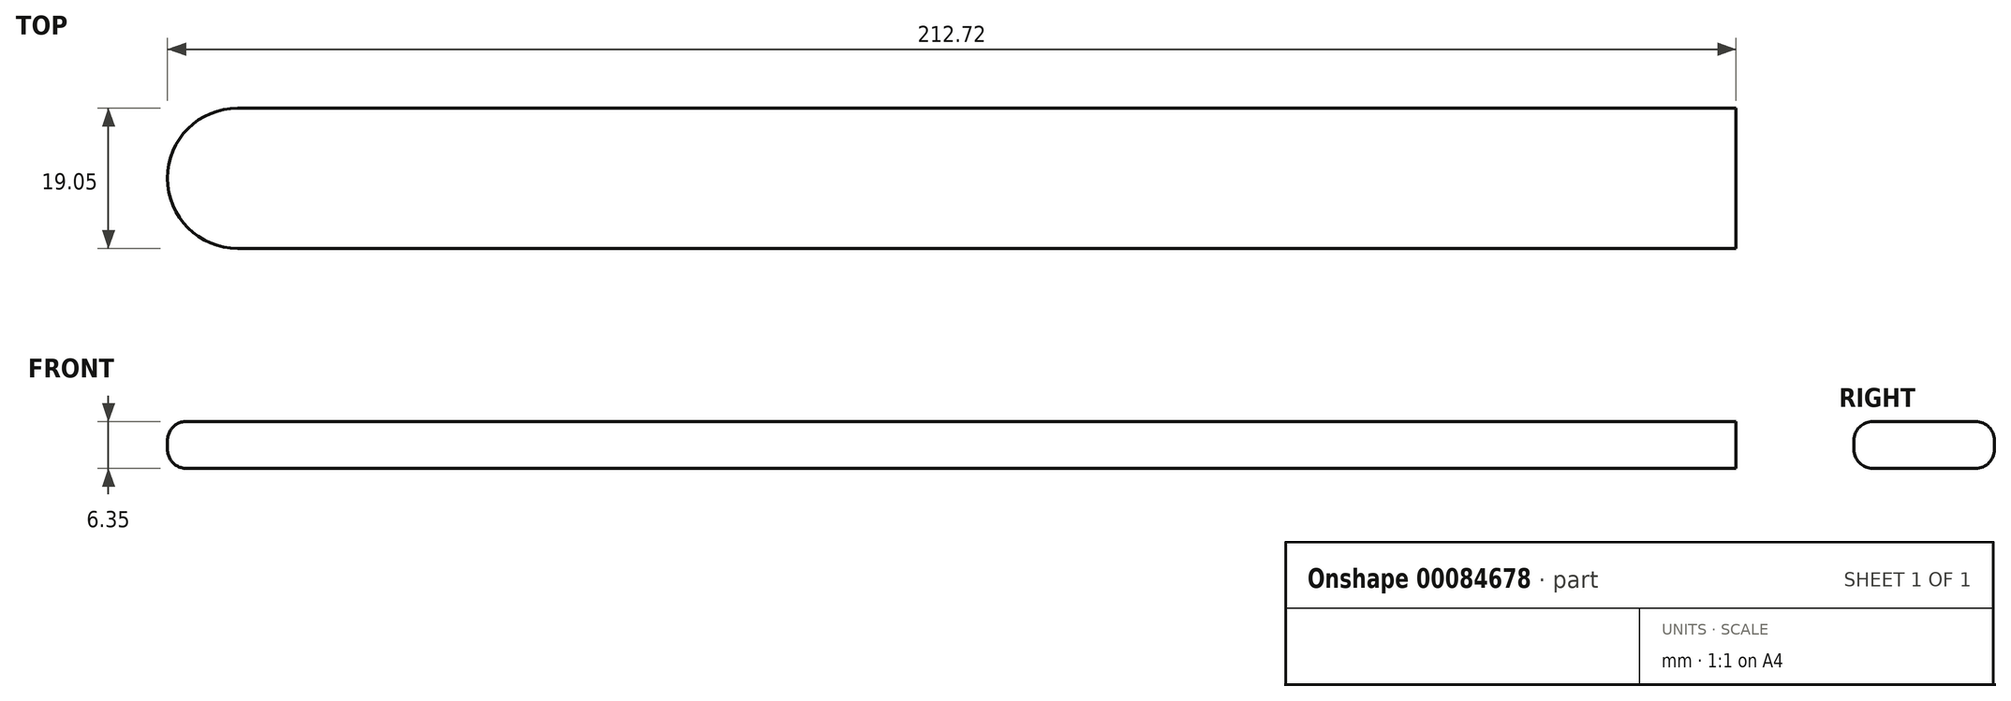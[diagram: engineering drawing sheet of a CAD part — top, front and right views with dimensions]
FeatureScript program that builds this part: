
annotation { "Feature Type Name" : "Feature", "Feature Type Description" : "" }
export const myFeature = defineFeature(function(context is Context, id is Id, definition is map)
    precondition{}
    {
        {
            var Q0;
            Q0=qCreatedBy(makeId("Top.planeOp"),FACE);
            var sketch = newSketch(context, id + "F0", { "sketchPlane" : qUnion([Q0])});
            skLineSegment(sketch, "E0", {"start": v(0, 0) * mm, "end": v(-203.2, 0) * mm});
            skLineSegment(sketch, "E1", {"start": v(0, 19.05) * mm, "end": v(-203.2, 19.05) * mm});
            skArc(sketch, "E2", {"start": v(-203.2, 19.05) * mm, "mid": v(-212.72, 9.52) * mm, "end": v(-203.2, 0) * mm});
            skLineSegment(sketch, "E3", {"start": v(0, 19.05) * mm, "end": v(0, 0) * mm});
            skSolve(sketch);
        }
        {
            var Q0;
            Q0=makeQuery(id+"F0.imprint","IMPRINT",FACE,{"disambiguationData":[TD([[makeQuery(id+"F0.imprint","IMPRINT",EDGE,{"derivedFrom":sQuery(id+"F0.wireOp",EDGE,"E0")}),-1.0]])]});
            extrude(context, id + "F1", {"entities" : qUnion([Q0]), "depth" : 6.35 * mm});
        }
        {
            var Q0;
            Q0=makeQuery(id+"F1.opExtrude","CAP_EDGE",EDGE,{"disambiguationData":[OSD([sQuery(id+"F0.wireOp",EDGE,"E1")])],"isStart":true});
            var Q1;
            Q1=makeQuery(id+"F1.opExtrude","CAP_EDGE",EDGE,{"disambiguationData":[OSD([sQuery(id+"F0.wireOp",EDGE,"E1")])],"isStart":false});
            fillet(context, id + "F2", {"entities" : qUnion([Q0, Q1]), "radius" : 2.54 * mm, "tangentPropagation" : true, "allowEdgeOverflow" : false});
        }
    });
